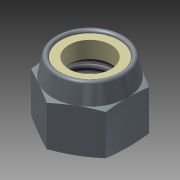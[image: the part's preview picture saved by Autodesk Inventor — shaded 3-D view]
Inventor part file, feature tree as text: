
AUTODESK INVENTOR PART (.ipt)
format: ipt  version: 2014 (Build 180170000, 170)  size: 193,024 bytes
history: native  units: mm (DEFAULTED — no unit token found)
features: sketch x5, extrude x2, revolve x2, other x1, plane x1, thread x1
ambient origin geometry x8: Origin, YZ Plane, XZ Plane, XY Plane, X Axis, Y Axis, Z Axis, Center Point
bodies: Solid1 (feature_tree)
feature tree (12):
  other  "Hexagon_flats_join1"
  extrude  "Extrusion1"  Depth=25.4mm TaperAngle=0.0deg
  revolve  "Revolution1"  Angle=90.0deg
  plane  "Work Plane1"
  extrude  "Extrusion2"  Depth=1.5875mm
  revolve  "Revolution2"  Angle=15.0deg
  thread  "Thread1"  [1 undecoded]
  sketch  "Sketch1"  dims[d0=14.2875mm d3=25.4mm d4=0.0mm]
  sketch  "Sketch2"  dims[d5=13.788101mm d7=90.0deg]
  sketch  "Sketch3"  dims[d9=25.4mm d10=0.0mm d11=1.5875mm]
  sketch  "Sketch4"  dims[d12=15.0deg d13=15.0deg d14=14.2875mm]
  sketch  "Sketch5"  dims[d15=90.0deg d16=25.4mm d17=0.0mm]
note: 1 required parameter value undecoded (feature->parameter linkage not recoverable at this tier; creation-order binding heuristic only, values carry confidence <= 0.55)
